# Revit family: Alcon-14087-Revit-Family
name_source: partatom
category: Lighting Fixtures
units: mm (PartAtom-declared; Revit-internal decimal feet)

## family parameters
Classification Number = 23.80.70.11.17
Cut with Voids When Loaded = No
Host = Face
Light Source = Yes
Maintain Annotation Orientation = No
Part Type = Normal
Room Calculation Point = No
Round Connector Dimension = Use Diameter
Shared = No

## types (1)
- 14087-4'
    Apparent Power = 62 VA
    Assembly Code = D5020200
    Color Filter = 16777215
    Connector Description = Connector for Electrical Power
    Date Updated = 2025/03/31
    Default Elevation = 4' - 0"
    Depth = 0' - 3 3/8"
    Description = High Efficiency LED for Recessed Installation
    Dimming Lamp Color Temperature Shift = <None>
    Emit Shape Visible in Rendering = No
    Emit from Rectangle Length = 4' - 0"
    Emit from Rectangle Width = 1' - 11 13/16"
    Housing Material = Aluminum - Powder Coated - White
    Lamp = LED
    Length = 4' - 0"
    Lens Material = Glass - Clear
    Load Classification = Lighting
    Manufacturer = Alcon Lighting
    Number of Poles = 1
    Operating Temperature = -40°C to +40°C (-40°F to +104°F)
    Photometric File Name = Default - please load Revit Family Type Catalog
    Photometric Web File = Select File (Match Photometric File Name)
    Power Factor = 0.95
    Product Documentation Link = https://www.alconlighting.com
    Product Name = LED Troffer Panel Light Recessed
    Product Page URL = https://www.alconlighting.com
    Rendering Note = For accurate photometric rendering please refer to LSI for instructions
    Tilt Angle = 90.00°
    URL = https://www.alconlighting.com
    Version = 2
    Voltage = 120 V
    Voltage Note = Universal voltage (120-277 Vac) Input 50/60 Hz
    Warranty URL = https://www.alconlighting.com
    Wattage Comments = 29 Watts - 59 Watts
    Watts = 59 W
    Weight = 0.00 lbf
    Width = 1' - 11 13/16"

## geometry (parser evidence)
native form markers: Sweep x6
no freeform markers — native parametric forms only
